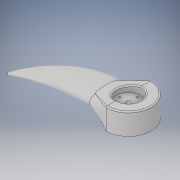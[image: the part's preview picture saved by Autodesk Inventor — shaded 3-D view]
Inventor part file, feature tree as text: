
AUTODESK INVENTOR PART (.ipt)
format: ipt  version: 2019 (Build 230136000, 136)  size: 370,176 bytes
history: native  units: mm
features: other x8, sketch x8, extrude x3, loft x2, fillet x2, revolve x1
ambient origin geometry x8: Origin, YZ Plane, XZ Plane, XY Plane, X Axis, Y Axis, Z Axis, Center Point
bodies: Body1 (feature_tree)
feature tree (24):
  other  "Твердое тело1"
  extrude  "Выдавливание1"  Depth=20.0mm TaperAngle=0.0deg
  other  "РабПлоскость5"
  loft  "Лофт3"
  other  "РабПлоскость6"
  sketch  "Эскиз11"
  revolve  "Вращение2"
  other  "РабПлоскость7"
  sketch  "Эскиз13"
  other  "РабПлоскость8"
  loft  "Лофт4"
  extrude  "Выдавливание5"  TaperAngle=0.0deg  [1 undecoded]
  extrude  "Выдавливание6"  [1 undecoded]
  fillet  "Сопряжение3"  Radius=100.0mm
  fillet  "Сопряжение4"  Radius=3.333333mm
  sketch  "Эскиз1"
  sketch  "Эскиз10"
  other  "Ребра4"
  sketch  "Эскиз12"
  sketch  "Эскиз14"
  other  "Ребра5"
  other  "Ребра6"
  sketch  "Эскиз16"
  sketch  "Эскиз17"
note: 2 required parameter values undecoded (feature->parameter linkage not recoverable at this tier; creation-order binding heuristic only, values carry confidence <= 0.55)
